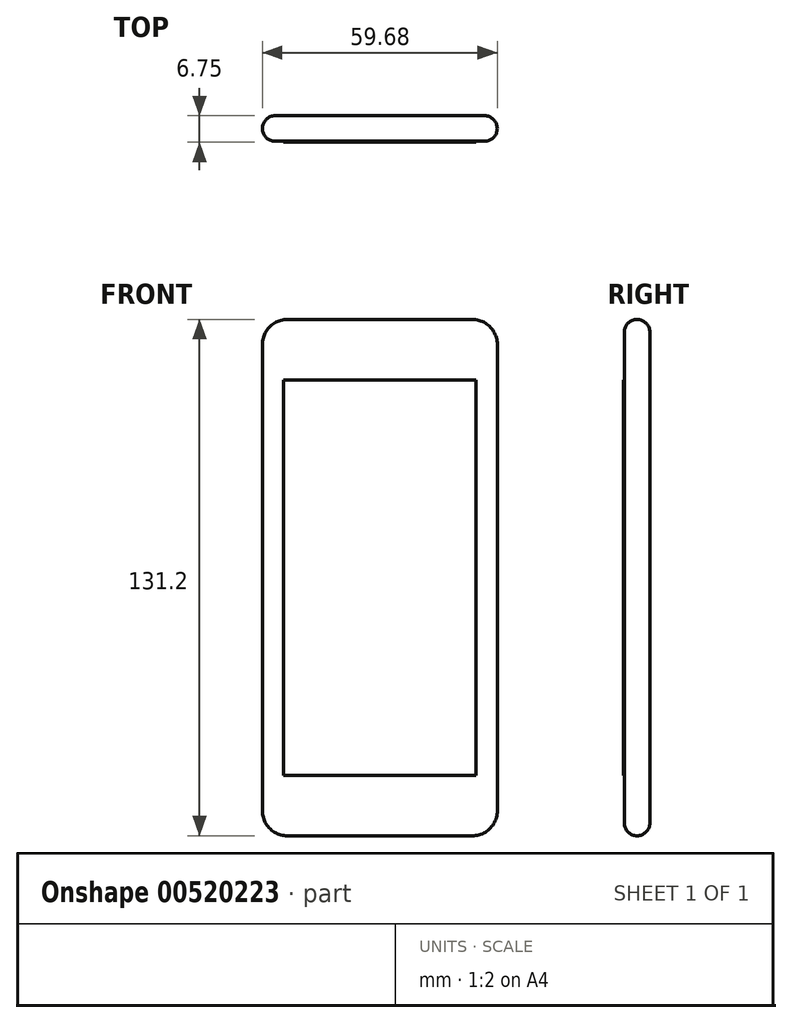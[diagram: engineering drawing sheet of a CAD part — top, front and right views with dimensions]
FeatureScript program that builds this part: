
annotation { "Feature Type Name" : "Feature", "Feature Type Description" : "" }
export const myFeature = defineFeature(function(context is Context, id is Id, definition is map)
    precondition{}
    {
        {
            var Q0;
            Q0=qCreatedBy(makeId("Front.planeOp"),FACE);
            var sketch = newSketch(context, id + "F0", { "sketchPlane" : qUnion([Q0])});
            skLineSegment(sketch, "E0.bottom", {"start": v(23.49, 65.6) * mm, "end": v(-23.49, 65.6) * mm});
            skLineSegment(sketch, "E0.top", {"start": v(23.49, -65.6) * mm, "end": v(-23.49, -65.6) * mm});
            skLineSegment(sketch, "E0.left", {"start": v(29.84, 59.25) * mm, "end": v(29.84, -59.25) * mm});
            skLineSegment(sketch, "E0.right", {"start": v(-29.84, 59.25) * mm, "end": v(-29.84, -59.25) * mm});
            skPoint(sketch, "E0.middle", {"position": v(0, 0) * mm});
            skPoint(sketch, "E1.visualSharp", {"position": v(-29.84, 65.6) * mm});
            skArc(sketch, "E1.filletArc", {"start": v(-23.49, 65.6) * mm, "mid": v(-27.98, 63.74) * mm, "end": v(-29.84, 59.25) * mm});
            skPoint(sketch, "E2.visualSharp", {"position": v(29.84, 65.6) * mm});
            skArc(sketch, "E2.filletArc", {"start": v(29.84, 59.25) * mm, "mid": v(27.98, 63.74) * mm, "end": v(23.49, 65.6) * mm});
            skPoint(sketch, "E3.visualSharp", {"position": v(-29.84, -65.6) * mm});
            skArc(sketch, "E3.filletArc", {"start": v(-29.84, -59.25) * mm, "mid": v(-27.98, -63.74) * mm, "end": v(-23.49, -65.6) * mm});
            skPoint(sketch, "E4.visualSharp", {"position": v(29.84, -65.6) * mm});
            skArc(sketch, "E4.filletArc", {"start": v(23.49, -65.6) * mm, "mid": v(27.98, -63.74) * mm, "end": v(29.84, -59.25) * mm});
            skSolve(sketch);
        }
        {
            var Q0;
            Q0=makeQuery(id+"F0.imprint","IMPRINT",FACE,{"disambiguationData":[TD([[makeQuery(id+"F0.imprint","IMPRINT",EDGE,{"derivedFrom":sQuery(id+"F0.wireOp",EDGE,"E0.bottom")}),1.0]])]});
            extrude(context, id + "F1", {"entities" : qUnion([Q0]), "depth" : 6.5 * mm, "offsetDistance" : 25.4 * mm});
        }
        {
            var Q0;
            Q0=makeQuery(id+"F1.opExtrude","CAP_EDGE",EDGE,{"disambiguationData":[OSD([sQuery(id+"F0.wireOp",EDGE,"E0.left")])],"isStart":true});
            var Q1;
            Q1=makeQuery(id+"F1.opExtrude","CAP_EDGE",EDGE,{"disambiguationData":[OSD([sQuery(id+"F0.wireOp",EDGE,"E0.left")])],"isStart":false});
            var Q2;
            Q2=makeQuery(id+"F1.opExtrude","CAP_EDGE",EDGE,{"disambiguationData":[OSD([sQuery(id+"F0.wireOp",EDGE,"E0.right")])],"isStart":false});
            var Q3;
            Q3=makeQuery(id+"F1.opExtrude","CAP_EDGE",EDGE,{"disambiguationData":[OSD([sQuery(id+"F0.wireOp",EDGE,"E0.bottom")])],"isStart":true});
            var Q4;
            Q4=makeQuery(id+"F1.opExtrude","CAP_EDGE",EDGE,{"disambiguationData":[OSD([sQuery(id+"F0.wireOp",EDGE,"E0.bottom")])],"isStart":false});
            var Q5;
            Q5=makeQuery(id+"F1.opExtrude","CAP_EDGE",EDGE,{"disambiguationData":[OSD([sQuery(id+"F0.wireOp",EDGE,"E1.filletArc")])],"isStart":false});
            var Q6;
            Q6=makeQuery(id+"F1.opExtrude","CAP_EDGE",EDGE,{"disambiguationData":[OSD([sQuery(id+"F0.wireOp",EDGE,"E1.filletArc")])],"isStart":true});
            var Q7;
            Q7=makeQuery(id+"F1.opExtrude","CAP_EDGE",EDGE,{"disambiguationData":[OSD([sQuery(id+"F0.wireOp",EDGE,"E2.filletArc")])],"isStart":false});
            var Q8;
            Q8=makeQuery(id+"F1.opExtrude","CAP_EDGE",EDGE,{"disambiguationData":[OSD([sQuery(id+"F0.wireOp",EDGE,"E2.filletArc")])],"isStart":true});
            var Q9;
            Q9=makeQuery(id+"F1.opExtrude","CAP_EDGE",EDGE,{"disambiguationData":[OSD([sQuery(id+"F0.wireOp",EDGE,"E4.filletArc")])],"isStart":false});
            var Q10;
            Q10=makeQuery(id+"F1.opExtrude","CAP_EDGE",EDGE,{"disambiguationData":[OSD([sQuery(id+"F0.wireOp",EDGE,"E0.top")])],"isStart":false});
            var Q11;
            Q11=makeQuery(id+"F1.opExtrude","CAP_EDGE",EDGE,{"disambiguationData":[OSD([sQuery(id+"F0.wireOp",EDGE,"E3.filletArc")])],"isStart":false});
            var Q12;
            Q12=makeQuery(id+"F1.opExtrude","CAP_EDGE",EDGE,{"disambiguationData":[OSD([sQuery(id+"F0.wireOp",EDGE,"E4.filletArc")])],"isStart":true});
            var Q13;
            Q13=makeQuery(id+"F1.opExtrude","CAP_EDGE",EDGE,{"disambiguationData":[OSD([sQuery(id+"F0.wireOp",EDGE,"E0.top")])],"isStart":true});
            var Q14;
            Q14=makeQuery(id+"F1.opExtrude","CAP_EDGE",EDGE,{"disambiguationData":[OSD([sQuery(id+"F0.wireOp",EDGE,"E3.filletArc")])],"isStart":true});
            var Q15;
            Q15=makeQuery(id+"F1.opExtrude","SWEPT_FACE",FACE,{"disambiguationData":[OSD([sQuery(id+"F0.wireOp",EDGE,"E0.right")])]});
            var Q16;
            Q16=makeQuery(id+"F1.opExtrude","CAP_EDGE",EDGE,{"disambiguationData":[OSD([sQuery(id+"F0.wireOp",EDGE,"E0.right")])],"isStart":true});
            fillet(context, id + "F2", {"entities" : qUnion([Q0, Q1, Q2, Q3, Q4, Q5, Q6, Q7, Q8, Q9, Q10, Q11, Q12, Q13, Q14, Q15, Q16]), "radius" : 3.25 * mm, "tangentPropagation" : true, "allowEdgeOverflow" : false});
        }
        {
            var Q0;
            Q0=qCreatedBy(makeId("Front.planeOp"),FACE);
            var sketch = newSketch(context, id + "F3", { "sketchPlane" : qUnion([Q0])});
            skLineSegment(sketch, "E5.bottom", {"start": v(-24.78, 48.36) * mm, "end": v(24.78, 48.36) * mm});
            skLineSegment(sketch, "E5.top", {"start": v(-24.78, -48.36) * mm, "end": v(24.78, -48.36) * mm});
            skLineSegment(sketch, "E5.left", {"start": v(-24.78, 48.36) * mm, "end": v(-24.78, -48.36) * mm});
            skLineSegment(sketch, "E5.right", {"start": v(24.78, 48.36) * mm, "end": v(24.78, -48.36) * mm});
            skPoint(sketch, "E5.middle", {"position": v(0, 0) * mm});
            skSolve(sketch);
        }
        {
            var Q0;
            Q0=sQuery(id+"F3.wireOp",EDGE,"E5.bottom");
            var Q1;
            Q1=sQuery(id+"F3.wireOp",EDGE,"E5.left");
            var Q2;
            Q2=sQuery(id+"F3.wireOp",EDGE,"E5.right");
            var Q3;
            Q3=sQuery(id+"F3.wireOp",EDGE,"E5.top");
            extrude(context, id + "F4", {"bodyType" : ToolBodyType.SURFACE, "surfaceEntities" : qUnion([Q0, Q1, Q2, Q3]), "depth" : 0.25 * mm, "offsetDistance" : 25.4 * mm});
        }
        {
            var Q0;
            Q0=qCreatedBy(makeId("Front.planeOp"),FACE);
            var sketch = newSketch(context, id + "F5", { "sketchPlane" : qUnion([Q0])});
            skCircle(sketch, "E6", {"center": v(0, -55.78) * mm, "radius": 4.2 * mm});
            skSolve(sketch);
        }
        {
            var Q0;
            Q0 = qSketchRegion(id + "F5", true);
            extrude(context, id + "F6", {"entities" : qUnion([Q0]), "operationType" : NewBodyOperationType.ADD, "depth" : 0.25 * mm, "offsetDistance" : 25.4 * mm});
        }
        {
            var Q0;
            Q0=makeQuery(id+"F1.opExtrude","CAP_FACE",FACE,{"disambiguationData":[OSD([sQuery(id+"F0.wireOp",EDGE,"E0.bottom"),sQuery(id+"F0.wireOp",EDGE,"E0.top"),sQuery(id+"F0.wireOp",EDGE,"E0.left"),sQuery(id+"F0.wireOp",EDGE,"E0.right"),sQuery(id+"F0.wireOp",EDGE,"E1.filletArc"),sQuery(id+"F0.wireOp",EDGE,"E2.filletArc"),sQuery(id+"F0.wireOp",EDGE,"E3.filletArc"),sQuery(id+"F0.wireOp",EDGE,"E4.filletArc")])],"isStart":false});
            var sketch = newSketch(context, id + "F7", { "sketchPlane" : qUnion([Q0])});
            skLineSegment(sketch, "E7.bottom", {"start": v(24.45, 50.23) * mm, "end": v(-24.45, 50.23) * mm});
            skLineSegment(sketch, "E7.top", {"start": v(24.45, -50.23) * mm, "end": v(-24.45, -50.23) * mm});
            skLineSegment(sketch, "E7.left", {"start": v(24.45, 50.23) * mm, "end": v(24.45, -50.23) * mm});
            skLineSegment(sketch, "E7.right", {"start": v(-24.45, 50.23) * mm, "end": v(-24.45, -50.23) * mm});
            skPoint(sketch, "E7.middle", {"position": v(0, 0) * mm});
            skSolve(sketch);
        }
        {
            var Q0;
            Q0 = qSketchRegion(id + "F7", true);
            extrude(context, id + "F8", {"entities" : qUnion([Q0]), "operationType" : NewBodyOperationType.ADD, "depth" : 0.25 * mm, "offsetDistance" : 25.4 * mm});
        }
    });
